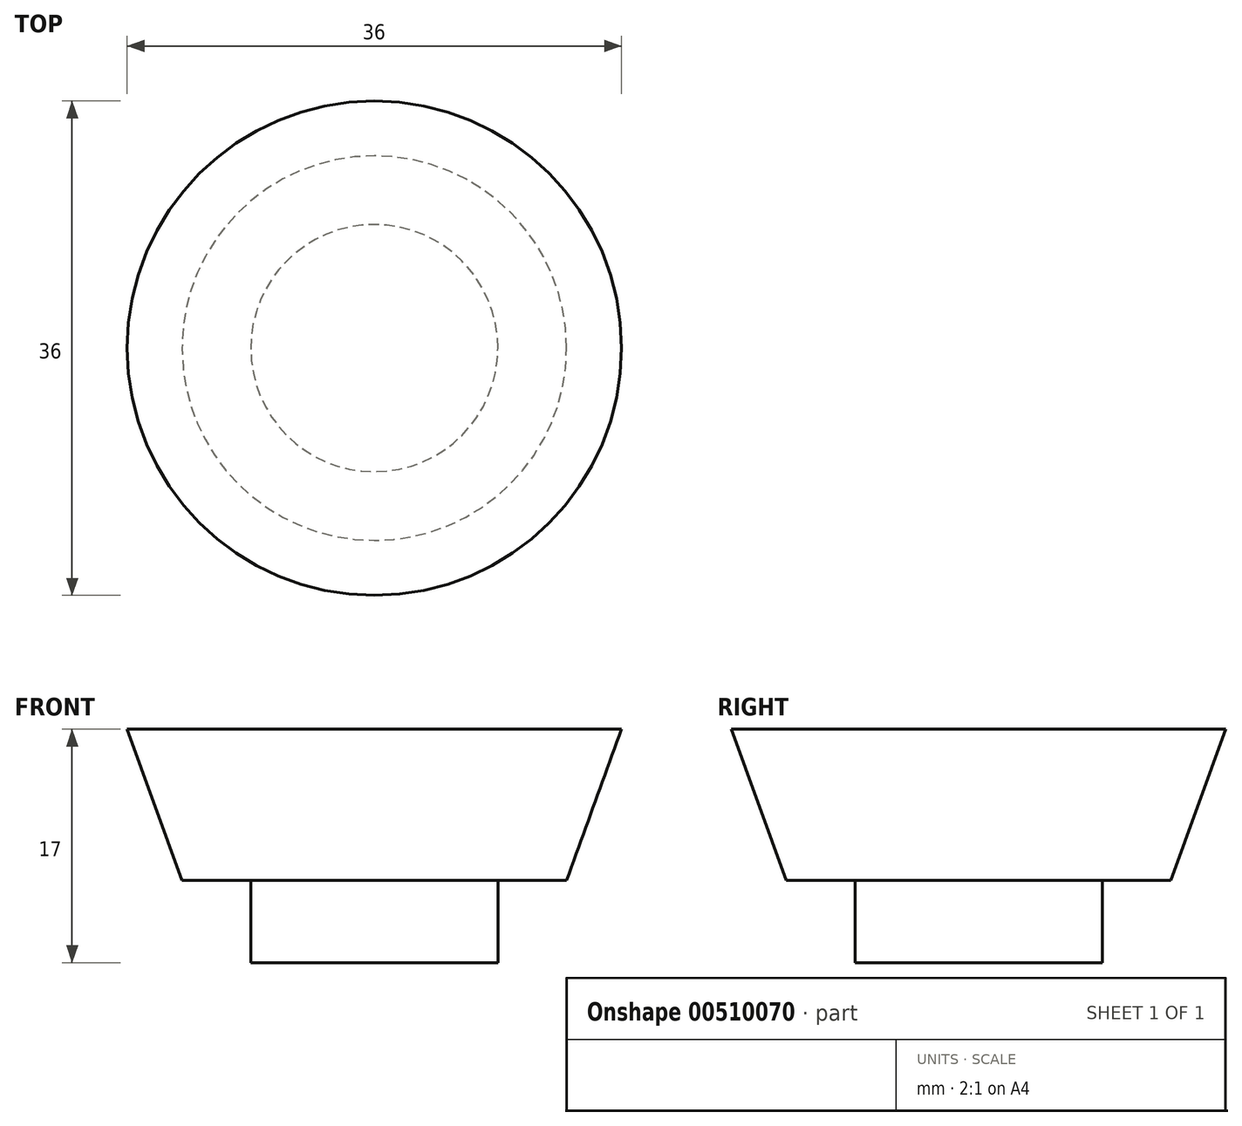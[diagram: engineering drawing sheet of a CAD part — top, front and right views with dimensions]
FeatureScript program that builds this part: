
annotation { "Feature Type Name" : "Feature", "Feature Type Description" : "" }
export const myFeature = defineFeature(function(context is Context, id is Id, definition is map)
    precondition{}
    {
        {
            var Q0;
            Q0=qCreatedBy(makeId("Top.planeOp"),FACE);
            var sketch = newSketch(context, id + "F0", { "sketchPlane" : qUnion([Q0])});
            skCircle(sketch, "E0", {"center": v(0, 0) * mm, "radius": 18 * mm});
            skSolve(sketch);
        }
        {
            var Q0;
            Q0=qCreatedBy(makeId("Top.planeOp"),FACE);
            cPlane(context, id + "F1", {"entities" : qUnion([Q0]), "cplaneType" : CPlaneType.OFFSET, "offset" : 11 * mm, "oppositeDirection" : true, "width" : 150 * mm, "height" : 150 * mm});
        }
        {
            var Q0;
            Q0=qCreatedBy(id+"F1.planeOp",FACE);
            var sketch = newSketch(context, id + "F2", { "sketchPlane" : qUnion([Q0])});
            skCircle(sketch, "E1", {"center": v(0, 0) * mm, "radius": 14 * mm});
            skSolve(sketch);
        }
        {
            var Q0;
            Q0=makeQuery(id+"F0.imprint","IMPRINT",FACE,{"disambiguationData":[TD([[makeQuery(id+"F0.imprint","IMPRINT",EDGE,{"derivedFrom":sQuery(id+"F0.wireOp",EDGE,"E0")}),1.0]])]});
            var Q1;
            Q1=makeQuery(id+"F2.imprint","IMPRINT",FACE,{"disambiguationData":[TD([[makeQuery(id+"F2.imprint","IMPRINT",EDGE,{"derivedFrom":sQuery(id+"F2.wireOp",EDGE,"E1")}),1.0]])]});
            loft(context, id + "F3", {"sheetProfilesArray" : [{ "sheetProfileEntities" : qUnion([Q0]) }, { "sheetProfileEntities" : qUnion([Q1]) }]});
        }
        {
            var Q0;
            Q0=makeQuery(id+"F3.opLoft","CAP_FACE",FACE,{"disambiguationData":[OSD([makeQuery(id+"F2.imprint","IMPRINT",FACE,{"disambiguationData":[TD([[makeQuery(id+"F2.imprint","IMPRINT",EDGE,{"derivedFrom":sQuery(id+"F2.wireOp",EDGE,"E1")}),1.0]])]})])],"isStart":true});
            var sketch = newSketch(context, id + "F4", { "sketchPlane" : qUnion([Q0])});
            skCircle(sketch, "E2", {"center": v(0, 0) * mm, "radius": 9 * mm});
            skSolve(sketch);
        }
        {
            var Q0;
            Q0=makeQuery(id+"F4.imprint","IMPRINT",FACE,{"disambiguationData":[TD([[makeQuery(id+"F4.imprint","IMPRINT",EDGE,{"derivedFrom":sQuery(id+"F4.wireOp",EDGE,"E2")}),1.0]])]});
            extrude(context, id + "F5", {"entities" : qUnion([Q0]), "operationType" : NewBodyOperationType.ADD, "depth" : 6 * mm});
        }
    });
